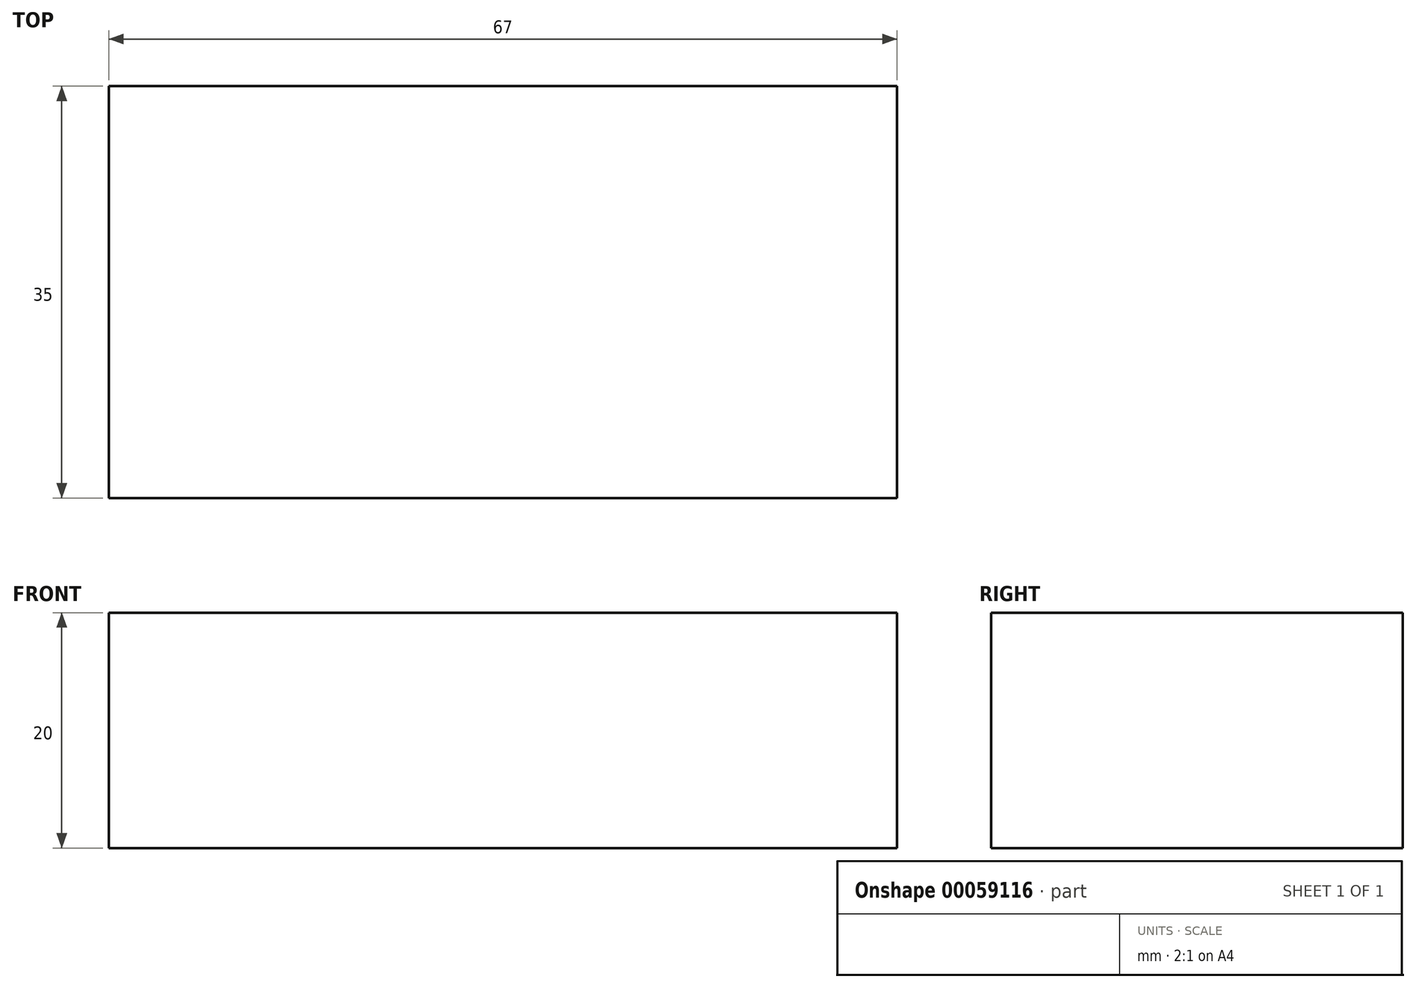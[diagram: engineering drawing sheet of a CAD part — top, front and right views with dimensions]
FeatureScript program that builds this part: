
annotation { "Feature Type Name" : "Feature", "Feature Type Description" : "" }
export const myFeature = defineFeature(function(context is Context, id is Id, definition is map)
    precondition{}
    {
        {
            var Q0;
            Q0=qCreatedBy(makeId("Top.planeOp"),FACE);
            var sketch = newSketch(context, id + "F0", { "sketchPlane" : qUnion([Q0])});
            skLineSegment(sketch, "E0.rect.bottom", {"start": v(33.5, 17.5) * mm, "end": v(-33.5, 17.5) * mm});
            skLineSegment(sketch, "E0.rect.top", {"start": v(33.5, -17.5) * mm, "end": v(-33.5, -17.5) * mm});
            skLineSegment(sketch, "E0.rect.left", {"start": v(33.5, 17.5) * mm, "end": v(33.5, -17.5) * mm});
            skLineSegment(sketch, "E0.rect.right", {"start": v(-33.5, 17.5) * mm, "end": v(-33.5, -17.5) * mm});
            skPoint(sketch, "E0.rect.middle", {"position": v(0, 0) * mm});
            skSolve(sketch);
        }
        {
            var Q0;
            Q0=qSketchRegion(id+"F0",true);
            extrude(context, id + "F1", {"entities" : qUnion([Q0]), "depth" : 20 * mm});
        }
    });
